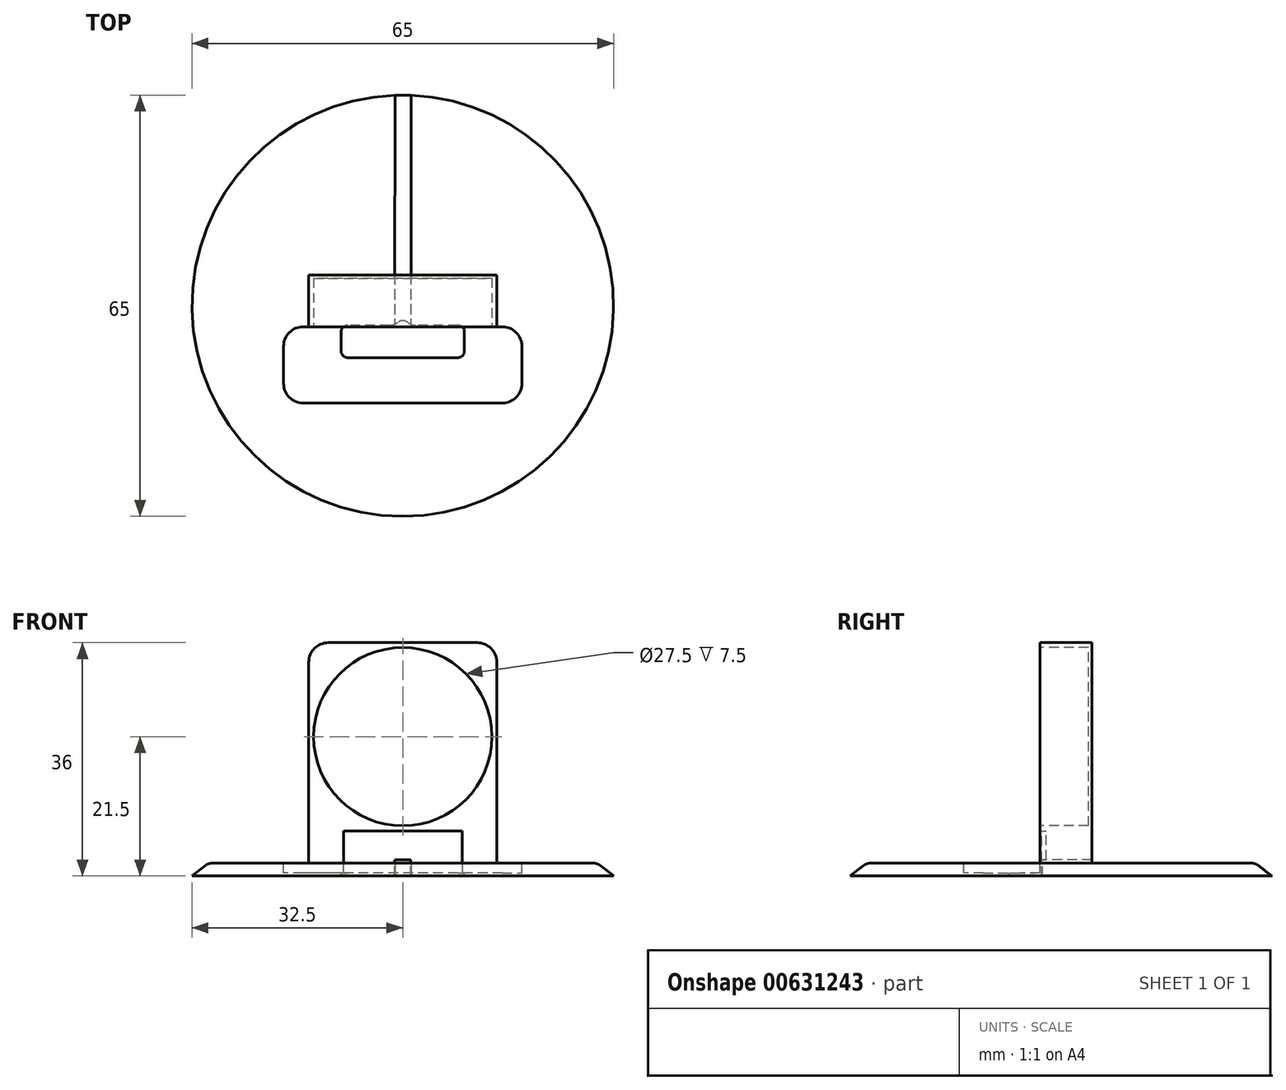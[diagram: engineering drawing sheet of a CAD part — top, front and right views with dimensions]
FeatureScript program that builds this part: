
annotation { "Feature Type Name" : "Feature", "Feature Type Description" : "" }
export const myFeature = defineFeature(function(context is Context, id is Id, definition is map)
    precondition{}
    {
        {
            var Q0;
            Q0=qCreatedBy(makeId("Top.planeOp"),FACE);
            var sketch = newSketch(context, id + "F0", { "sketchPlane" : qUnion([Q0])});
            skCircle(sketch, "E0", {"center": v(0, 0) * mm, "radius": 32.5 * mm});
            skSolve(sketch);
        }
        {
            var Q0;
            Q0=qCreatedBy(makeId("Top.planeOp"),FACE);
            cPlane(context, id + "F1", {"entities" : qUnion([Q0]), "cplaneType" : CPlaneType.OFFSET, "offset" : 2 * mm, "width" : 152.4 * mm, "height" : 152.4 * mm});
        }
        {
            var Q0;
            Q0=qCreatedBy(id+"F1.planeOp",FACE);
            var sketch = newSketch(context, id + "F2", { "sketchPlane" : qUnion([Q0])});
            skCircle(sketch, "E1", {"center": v(0, 0) * mm, "radius": 30 * mm});
            skSolve(sketch);
        }
        {
            var Q0;
            Q0 = qSketchRegion(id + "F0", true);
            var Q1;
            Q1 = qSketchRegion(id + "F2", true);
            loft(context, id + "F3", {"sheetProfilesArray" : [{ "sheetProfileEntities" : qUnion([Q0]) }, { "sheetProfileEntities" : qUnion([Q1]) }]});
        }
        {
            var Q0;
            Q0=makeQuery(id+"F3.opLoft","CAP_FACE",FACE,{"disambiguationData":[OSD([makeQuery(id+"F2.imprint","IMPRINT",FACE,{"disambiguationData":[TD([[makeQuery(id+"F2.imprint","IMPRINT",EDGE,{"derivedFrom":sQuery(id+"F2.wireOp",EDGE,"E1")}),1.0]])]})])],"isStart":true});
            var sketch = newSketch(context, id + "F4", { "sketchPlane" : qUnion([Q0])});
            skLineSegment(sketch, "E2.bottom", {"start": v(18.38, -15) * mm, "end": v(-18.38, -15) * mm});
            skLineSegment(sketch, "E2.top", {"start": v(18.38, -3.25) * mm, "end": v(-18.38, -3.25) * mm});
            skLineSegment(sketch, "E2.left", {"start": v(18.38, -15) * mm, "end": v(18.37, -3.25) * mm});
            skLineSegment(sketch, "E2.right", {"start": v(-18.38, -15) * mm, "end": v(-18.38, -3.25) * mm});
            skPoint(sketch, "E2.middle", {"position": v(0, -9.13) * mm});
            skSolve(sketch);
        }
        {
            var Q0;
            Q0 = qSketchRegion(id + "F4", true);
            extrude(context, id + "F5", {"entities" : qUnion([Q0]), "operationType" : NewBodyOperationType.REMOVE, "oppositeDirection" : true, "depth" : 1.5 * mm, "offsetDistance" : 25.4 * mm});
        }
        {
            var Q0;
            Q0=makeQuery(id+"F5.boolean.opBoolean","COPY",EDGE,{"derivedFrom":makeQuery(id+"F5.opExtrude","SWEPT_EDGE",EDGE,{"disambiguationData":[OSD([sQuery(id+"F4.wireOp",EDGE,"E2.top"),sQuery(id+"F4.wireOp",EDGE,"E2.right")])]})});
            var Q1;
            Q1=makeQuery(id+"F5.boolean.opBoolean","COPY",EDGE,{"derivedFrom":makeQuery(id+"F5.opExtrude","SWEPT_EDGE",EDGE,{"disambiguationData":[OSD([sQuery(id+"F4.wireOp",EDGE,"E2.bottom"),sQuery(id+"F4.wireOp",EDGE,"E2.right")])]})});
            var Q2;
            Q2=makeQuery(id+"F5.boolean.opBoolean","COPY",EDGE,{"derivedFrom":makeQuery(id+"F5.opExtrude","SWEPT_EDGE",EDGE,{"disambiguationData":[OSD([sQuery(id+"F4.wireOp",EDGE,"E2.bottom"),sQuery(id+"F4.wireOp",EDGE,"E2.left")])]})});
            var Q3;
            Q3=makeQuery(id+"F5.boolean.opBoolean","COPY",EDGE,{"derivedFrom":makeQuery(id+"F5.opExtrude","SWEPT_EDGE",EDGE,{"disambiguationData":[OSD([sQuery(id+"F4.wireOp",EDGE,"E2.top"),sQuery(id+"F4.wireOp",EDGE,"E2.left")])]})});
            fillet(context, id + "F6", {"entities" : qUnion([Q0, Q1, Q2, Q3]), "radius" : 3 * mm, "tangentPropagation" : true, "allowEdgeOverflow" : false});
        }
        {
            var Q0;
            Q0=makeQuery(id+"F3.opLoft","CAP_FACE",FACE,{"disambiguationData":[OSD([makeQuery(id+"F2.imprint","IMPRINT",FACE,{"disambiguationData":[TD([[makeQuery(id+"F2.imprint","IMPRINT",EDGE,{"derivedFrom":sQuery(id+"F2.wireOp",EDGE,"E1")}),1.0]])]})])],"isStart":true});
            var sketch = newSketch(context, id + "F7", { "sketchPlane" : qUnion([Q0])});
            skLineSegment(sketch, "E3.bottom", {"start": v(14.5, -3.25) * mm, "end": v(-14.5, -3.25) * mm});
            skLineSegment(sketch, "E3.top", {"start": v(14.5, 4.75) * mm, "end": v(-14.5, 4.75) * mm});
            skLineSegment(sketch, "E3.left", {"start": v(14.5, -3.25) * mm, "end": v(14.5, 4.75) * mm});
            skLineSegment(sketch, "E3.right", {"start": v(-14.5, -3.25) * mm, "end": v(-14.5, 4.75) * mm});
            skPoint(sketch, "E3.middle", {"position": v(0, 0.75) * mm});
            skSolve(sketch);
        }
        {
            var Q0;
            Q0 = qSketchRegion(id + "F7", true);
            extrude(context, id + "F8", {"entities" : qUnion([Q0]), "operationType" : NewBodyOperationType.ADD, "depth" : 34 * mm, "offsetDistance" : 25.4 * mm});
        }
        {
            var Q0;
            Q0=makeQuery(id+"F8.boolean.opBoolean","MERGE",FACE,{"derivedFrom":[makeQuery(id+"F5.boolean.opBoolean","COPY",FACE,{"derivedFrom":makeQuery(id+"F5.opExtrude","SWEPT_FACE",FACE,{"disambiguationData":[OSD([sQuery(id+"F4.wireOp",EDGE,"E2.top")])]})}),makeQuery(id+"F8.opExtrude","SWEPT_FACE",FACE,{"disambiguationData":[OSD([sQuery(id+"F7.wireOp",EDGE,"E3.bottom")])]})]});
            var sketch = newSketch(context, id + "F9", { "sketchPlane" : qUnion([Q0])});
            skCircle(sketch, "E4", {"center": v(0, 21.5) * mm, "radius": 13.75 * mm});
            skSolve(sketch);
        }
        {
            var Q0;
            Q0 = qSketchRegion(id + "F9", true);
            extrude(context, id + "F10", {"entities" : qUnion([Q0]), "operationType" : NewBodyOperationType.REMOVE, "oppositeDirection" : true, "depth" : 7.5 * mm, "offsetDistance" : 25.4 * mm});
        }
        {
            var Q0;
            Q0=makeQuery(id+"F3.opLoft","MID_CAP_EDGE",EDGE,{"disambiguationData":[OSD([sQuery(id+"F0.wireOp",EDGE,"HcsIj851-Hvik-L4HQ-4wfW-GLEw0P9UqXFT"),sQuery(id+"F2.wireOp",EDGE,"E1")])],"capPos":1.0});
            fillet(context, id + "F11", {"entities" : qUnion([Q0]), "radius" : 2 * mm, "tangentPropagation" : true, "allowEdgeOverflow" : false});
        }
        {
            var Q0;
            Q0=makeQuery(id+"F8.opExtrude","CAP_EDGE",EDGE,{"disambiguationData":[OSD([sQuery(id+"F7.wireOp",EDGE,"E3.right")])],"isStart":false});
            var Q1;
            Q1=makeQuery(id+"F8.opExtrude","CAP_EDGE",EDGE,{"disambiguationData":[OSD([sQuery(id+"F7.wireOp",EDGE,"E3.left")])],"isStart":false});
            var Q2;
            Q2=makeQuery(id+"F8.opExtrude","CAP_EDGE",EDGE,{"disambiguationData":[OSD([sQuery(id+"F7.wireOp",EDGE,"E3.right")])],"isStart":true});
            var Q3;
            Q3=makeQuery(id+"F8.opExtrude","CAP_EDGE",EDGE,{"disambiguationData":[OSD([sQuery(id+"F7.wireOp",EDGE,"E3.left")])],"isStart":true});
            fillet(context, id + "F12", {"entities" : qUnion([Q0, Q1, Q2, Q3]), "radius" : 3 * mm, "tangentPropagation" : true, "allowEdgeOverflow" : false});
        }
        {
            var Q0;
            Q0=makeQuery(id+"F3.opLoft","CAP_FACE",FACE,{"disambiguationData":[OSD([makeQuery(id+"F2.imprint","IMPRINT",FACE,{"disambiguationData":[TD([[makeQuery(id+"F2.imprint","IMPRINT",EDGE,{"derivedFrom":sQuery(id+"F2.wireOp",EDGE,"E1")}),1.0]])]})])],"isStart":true});
            cPlane(context, id + "F13", {"entities" : qUnion([Q0]), "cplaneType" : CPlaneType.OFFSET, "offset" : 4.93 * mm, "width" : 152.4 * mm, "height" : 152.4 * mm});
        }
        {
            var Q0;
            Q0=qCreatedBy(id+"F13.planeOp",FACE);
            var sketch = newSketch(context, id + "F14", { "sketchPlane" : qUnion([Q0])});
            skCircle(sketch, "E5", {"center": v(0, -3.56) * mm, "radius": 1.25 * mm});
            skSolve(sketch);
        }
        {
            var Q0;
            Q0 = qSketchRegion(id + "F14", true);
            extrude(context, id + "F15", {"entities" : qUnion([Q0]), "operationType" : NewBodyOperationType.REMOVE, "oppositeDirection" : true, "depth" : 25.4 * mm, "offsetDistance" : 25.4 * mm});
        }
        {
            var Q0;
            Q0=qCreatedBy(id+"F13.planeOp",FACE);
            var sketch = newSketch(context, id + "F16", { "sketchPlane" : qUnion([Q0])});
            skLineSegment(sketch, "E6.bottom", {"start": v(9.5, -8) * mm, "end": v(-9.5, -8) * mm});
            skLineSegment(sketch, "E6.top", {"start": v(9.5, -3) * mm, "end": v(-9.5, -3) * mm});
            skLineSegment(sketch, "E6.left", {"start": v(9.5, -8) * mm, "end": v(9.5, -3) * mm});
            skLineSegment(sketch, "E6.right", {"start": v(-9.5, -8) * mm, "end": v(-9.5, -3) * mm});
            skPoint(sketch, "E6.middle", {"position": v(0, -5.5) * mm});
            skSolve(sketch);
        }
        {
            var Q0;
            Q0 = qSketchRegion(id + "F16", true);
            extrude(context, id + "F17", {"entities" : qUnion([Q0]), "operationType" : NewBodyOperationType.REMOVE, "oppositeDirection" : true, "depth" : 25.4 * mm, "offsetDistance" : 25.4 * mm});
        }
        {
            var Q0;
            Q0=makeQuery(id+"F17.boolean.opBoolean","COPY",EDGE,{"derivedFrom":makeQuery(id+"F17.opExtrude","SWEPT_EDGE",EDGE,{"disambiguationData":[OSD([sQuery(id+"F16.wireOp",EDGE,"E6.bottom"),sQuery(id+"F16.wireOp",EDGE,"E6.left")])]})});
            var Q1;
            Q1=makeQuery(id+"F17.boolean.opBoolean","COPY",EDGE,{"derivedFrom":makeQuery(id+"F17.opExtrude","SWEPT_EDGE",EDGE,{"disambiguationData":[OSD([sQuery(id+"F16.wireOp",EDGE,"E6.bottom"),sQuery(id+"F16.wireOp",EDGE,"E6.right")])]})});
            var Q2;
            Q2=makeQuery(id+"F17.boolean.opBoolean","COPY",EDGE,{"derivedFrom":makeQuery(id+"F17.opExtrude","SWEPT_EDGE",EDGE,{"disambiguationData":[OSD([sQuery(id+"F16.wireOp",EDGE,"E6.top"),sQuery(id+"F16.wireOp",EDGE,"E6.right")])]})});
            var Q3;
            Q3=makeQuery(id+"F17.boolean.opBoolean","COPY",EDGE,{"derivedFrom":makeQuery(id+"F17.opExtrude","SWEPT_EDGE",EDGE,{"disambiguationData":[OSD([sQuery(id+"F16.wireOp",EDGE,"E6.top"),sQuery(id+"F16.wireOp",EDGE,"E6.left")])]})});
            fillet(context, id + "F18", {"entities" : qUnion([Q0, Q1, Q2, Q3]), "radius" : 1 * mm, "tangentPropagation" : true, "allowEdgeOverflow" : false});
        }
        {
            var Q0;
            Q0=makeQuery(id+"F3.opLoft","CAP_FACE",FACE,{"disambiguationData":[OSD([makeQuery(id+"F0.imprint","IMPRINT",FACE,{"disambiguationData":[TD([[makeQuery(id+"F0.imprint","IMPRINT",EDGE,{"derivedFrom":sQuery(id+"F0.wireOp",EDGE,"E0")}),1.0]])]})])],"isStart":true});
            var sketch = newSketch(context, id + "F19", { "sketchPlane" : qUnion([Q0])});
            skLineSegment(sketch, "E7.bottom", {"start": v(1.3, -32.47) * mm, "end": v(-1.2, -32.48) * mm});
            skLineSegment(sketch, "E7.left", {"start": v(1.3, -32.47) * mm, "end": v(1.25, 3) * mm});
            skLineSegment(sketch, "E7.right", {"start": v(-1.2, -32.48) * mm, "end": v(-1.25, 3) * mm});
            skPoint(sketch, "E7.middle", {"position": v(0, 0) * mm});
            skLineSegment(sketch, "E8", {"start": v(-1.25, 3) * mm, "end": v(1.25, 3) * mm});
            skPoint(sketch, "E9.orphan", {"position": v(-1.3, 32.47) * mm});
            skPoint(sketch, "E10.orphan", {"position": v(1.2, 32.48) * mm});
            skSolve(sketch);
        }
        {
            var Q0;
            Q0 = qSketchRegion(id + "F19", true);
            extrude(context, id + "F20", {"entities" : qUnion([Q0]), "operationType" : NewBodyOperationType.REMOVE, "oppositeDirection" : true, "depth" : 2.5 * mm, "offsetDistance" : 25.4 * mm});
        }
        {
            var Q0;
            Q0=makeQuery(id+"F17.boolean.opBoolean","INTERSECT",EDGE,{"disambiguationData":[OD(1.0)],"derivedFrom":[makeQuery(id+"F15.boolean.opBoolean","COPY",FACE,{"derivedFrom":makeQuery(id+"F15.opExtrude","SWEPT_FACE",FACE,{"disambiguationData":[OSD([sQuery(id+"F14.wireOp",EDGE,"E5")])]})}),makeQuery(id+"F17.opExtrude","SWEPT_FACE",FACE,{"disambiguationData":[OSD([sQuery(id+"F16.wireOp",EDGE,"E6.top")])]})]});
            var Q1;
            Q1=makeQuery(id+"F17.boolean.opBoolean","INTERSECT",EDGE,{"disambiguationData":[OD(0.0)],"derivedFrom":[makeQuery(id+"F15.boolean.opBoolean","COPY",FACE,{"derivedFrom":makeQuery(id+"F15.opExtrude","SWEPT_FACE",FACE,{"disambiguationData":[OSD([sQuery(id+"F14.wireOp",EDGE,"E5")])]})}),makeQuery(id+"F17.opExtrude","SWEPT_FACE",FACE,{"disambiguationData":[OSD([sQuery(id+"F16.wireOp",EDGE,"E6.top")])]})]});
            fillet(context, id + "F21", {"entities" : qUnion([Q0, Q1]), "radius" : 2 * mm, "tangentPropagation" : true, "allowEdgeOverflow" : false});
        }
    });
